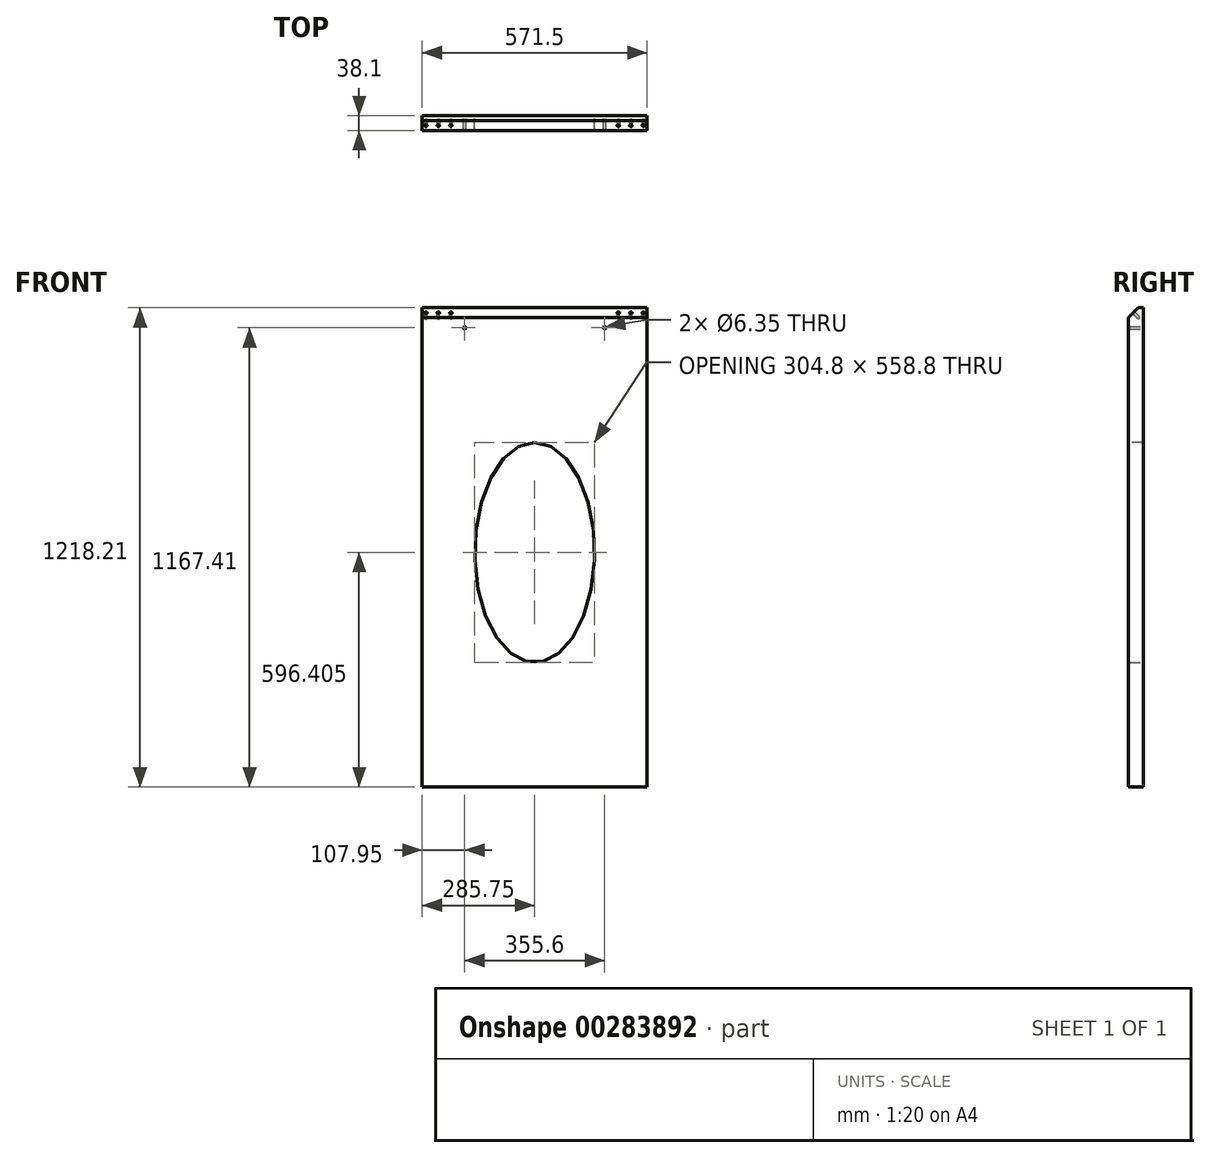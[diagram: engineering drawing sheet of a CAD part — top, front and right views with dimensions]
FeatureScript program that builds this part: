
annotation { "Feature Type Name" : "Feature", "Feature Type Description" : "" }
export const myFeature = defineFeature(function(context is Context, id is Id, definition is map)
    precondition{}
    {
        {
            var Q0;
            Q0=qCreatedBy(makeId("Front.planeOp"),FACE);
            var sketch = newSketch(context, id + "F0", { "sketchPlane" : qUnion([Q0])});
            skLineSegment(sketch, "E0.bottom", {"start": v(0, 0) * mm, "end": v(571.5, 0) * mm});
            skLineSegment(sketch, "E0.top", {"start": v(0, 1218.2) * mm, "end": v(571.5, 1218.2) * mm});
            skLineSegment(sketch, "E0.left", {"start": v(0, 0) * mm, "end": v(0, 1218.2) * mm});
            skLineSegment(sketch, "E0.right", {"start": v(571.5, 0) * mm, "end": v(571.5, 1218.2) * mm});
            skSolve(sketch);
        }
        {
            var Q0;
            Q0 = qSketchRegion(id + "F0", true);
            extrude(context, id + "F1", {"entities" : qUnion([Q0]), "depth" : 38.1 * mm});
        }
        {
            var Q0;
            Q0=makeQuery(id+"F1.opExtrude","CAP_EDGE",EDGE,{"disambiguationData":[OSD([sQuery(id+"F0.wireOp",EDGE,"E0.top")])],"isStart":false});
            chamfer(context, id + "F2", {"entities" : qUnion([Q0]), "width" : 25.4 * mm, "tangentPropagation" : true});
        }
        {
            var Q0;
            Q0=makeQuery(id+"F2.opChamfer","BLEND_FACE",FACE,{"disambiguationData":[OSD([sQuery(id+"F0.wireOp",EDGE,"E0.top")])]});
            var sketch = newSketch(context, id + "F3", { "sketchPlane" : qUnion([Q0])});
            skPoint(sketch, "E1", {"position": v(9.52, 834.46) * mm});
            skPoint(sketch, "E1.positionSnap0", {"position": v(0, 834.46) * mm});
            skPoint(sketch, "E2", {"position": v(41.27, 834.46) * mm});
            skPoint(sketch, "E3", {"position": v(73.03, 834.46) * mm});
            skPoint(sketch, "E4", {"position": v(285.75, 834.46) * mm});
            skLineSegment(sketch, "E5", {"start": v(285.75, 852.42) * mm, "end": v(285.75, 816.5) * mm, "construction": true});
            skPoint(sketch, "E6.MirrorP", {"position": v(498.47, 834.46) * mm});
            skPoint(sketch, "E7.MirrorP", {"position": v(530.22, 834.46) * mm});
            skPoint(sketch, "E8.MirrorP", {"position": v(561.97, 834.46) * mm});
            skSolve(sketch);
        }
        {
            var Q0;
            Q0=sQuery(id+"F3.wireOp",VERTEX,"E1");
            var Q1;
            Q1=sQuery(id+"F3.wireOp",VERTEX,"E2");
            var Q2;
            Q2=sQuery(id+"F3.wireOp",VERTEX,"E3");
            var Q3;
            Q3=sQuery(id+"F3.wireOp",VERTEX,"E6.MirrorP");
            var Q4;
            Q4=sQuery(id+"F3.wireOp",VERTEX,"E7.MirrorP");
            var Q5;
            Q5=sQuery(id+"F3.wireOp",VERTEX,"E8.MirrorP");
            var Q6;
            Q6=makeQuery(id+"F1.opExtrude","SWEPT_BODY",BODY,{"disambiguationData":[OSD([sQuery(id+"F0.wireOp",EDGE,"E0.bottom"),sQuery(id+"F0.wireOp",EDGE,"E0.top"),sQuery(id+"F0.wireOp",EDGE,"E0.left"),sQuery(id+"F0.wireOp",EDGE,"E0.right")])]});
            hole(context, id + "F4", {"style" : HoleStyle.SIMPLE, "endStyle" : HoleEndStyle.BLIND, "holeDiameter" : 6.35 * mm, "holeDepth" : 19.05 * mm, "tappedDepth" : 12.7 * mm, "tapClearance" : 3, "locations" : qUnion([Q0, Q1, Q2, Q3, Q4, Q5]), "scope" : qUnion([Q6])});
        }
        {
            var Q0;
            Q0=makeQuery(id+"F1.opExtrude","CAP_FACE",FACE,{"disambiguationData":[OSD([sQuery(id+"F0.wireOp",EDGE,"E0.bottom"),sQuery(id+"F0.wireOp",EDGE,"E0.top"),sQuery(id+"F0.wireOp",EDGE,"E0.left"),sQuery(id+"F0.wireOp",EDGE,"E0.right")])],"isStart":false});
            var sketch = newSketch(context, id + "F5", { "sketchPlane" : qUnion([Q0])});
            skPoint(sketch, "E9", {"position": v(19.05, 188.6) * mm});
            skPoint(sketch, "E10", {"position": v(552.45, 188.6) * mm});
            skLineSegment(sketch, "E11", {"start": v(0, 596.4) * mm, "end": v(571.5, 596.4) * mm});
            skLineSegment(sketch, "E12", {"start": v(285.75, 1192.8) * mm, "end": v(285.75, 0) * mm});
            skEllipse(sketch, "E13", {"center": v(285.75, 596.4) * mm, "majorRadius": 279.4 * mm, "minorRadius": 152.4 * mm, "majorAxis": v(0, 1)});
            skSolve(sketch);
        }
        {
            var Q0;
            {var subQ0=sQuery(id+"F5.wireOp",EDGE,"E13");var subQ1=sQuery(id+"F5.wireOp",EDGE,"E11");var subQ2=makeQuery(id+"F5.imprint","INTERSECT",VERTEX,{"disambiguationData":[OD(0.0)],"derivedFrom":[subQ1,subQ0]});Q0=makeQuery(id+"F5.imprint","IMPRINT",FACE,{"disambiguationData":[TD([[makeQuery(id+"F5.imprint","IMPRINT",EDGE,{"disambiguationData":[TD([[subQ2,-1.0]])],"derivedFrom":subQ1}),1.0]])]});}
            var Q1;
            {var subQ0=sQuery(id+"F5.wireOp",EDGE,"E12");var subQ1=sQuery(id+"F5.wireOp",EDGE,"E11");var subQ2=makeQuery(id+"F5.imprint","INTERSECT",VERTEX,{"derivedFrom":[subQ1,subQ0]});Q1=makeQuery(id+"F5.imprint","IMPRINT",FACE,{"disambiguationData":[TD([[makeQuery(id+"F5.imprint","IMPRINT",EDGE,{"disambiguationData":[TD([[subQ2,-1.0]])],"derivedFrom":subQ1}),1.0]])]});}
            var Q2;
            {var subQ0=sQuery(id+"F5.wireOp",EDGE,"E12");var subQ1=sQuery(id+"F5.wireOp",EDGE,"E11");var subQ2=makeQuery(id+"F5.imprint","INTERSECT",VERTEX,{"derivedFrom":[subQ1,subQ0]});Q2=makeQuery(id+"F5.imprint","IMPRINT",FACE,{"disambiguationData":[TD([[makeQuery(id+"F5.imprint","IMPRINT",EDGE,{"disambiguationData":[TD([[subQ2,-1.0]])],"derivedFrom":subQ1}),-1.0]])]});}
            var Q3;
            {var subQ0=sQuery(id+"F5.wireOp",EDGE,"E13");var subQ1=sQuery(id+"F5.wireOp",EDGE,"E11");var subQ2=makeQuery(id+"F5.imprint","INTERSECT",VERTEX,{"disambiguationData":[OD(0.0)],"derivedFrom":[subQ1,subQ0]});Q3=makeQuery(id+"F5.imprint","IMPRINT",FACE,{"disambiguationData":[TD([[makeQuery(id+"F5.imprint","IMPRINT",EDGE,{"disambiguationData":[TD([[subQ2,-1.0]])],"derivedFrom":subQ1}),-1.0]])]});}
            extrude(context, id + "F6", {"entities" : qUnion([Q0, Q1, Q2, Q3]), "operationType" : NewBodyOperationType.REMOVE, "endBound" : BoundingType.THROUGH_ALL, "oppositeDirection" : true, "depth" : 25.4 * mm});
        }
        {
            var Q0;
            Q0=makeQuery(id+"F1.opExtrude","CAP_FACE",FACE,{"disambiguationData":[OSD([sQuery(id+"F0.wireOp",EDGE,"E0.bottom"),sQuery(id+"F0.wireOp",EDGE,"E0.top"),sQuery(id+"F0.wireOp",EDGE,"E0.left"),sQuery(id+"F0.wireOp",EDGE,"E0.right")])],"isStart":true});
            var sketch = newSketch(context, id + "F7", { "sketchPlane" : qUnion([Q0])});
            skPoint(sketch, "E14", {"position": v(-463.55, 1167.4) * mm});
            skPoint(sketch, "E15.MirrorP", {"position": v(-107.95, 1167.4) * mm});
            skSolve(sketch);
        }
        {
            var Q0;
            Q0=sQuery(id+"F7.wireOp",VERTEX,"E14");
            var Q1;
            Q1=sQuery(id+"F7.wireOp",VERTEX,"E15.MirrorP");
            var Q2;
            Q2=makeQuery(id+"F1.opExtrude","SWEPT_BODY",BODY,{"disambiguationData":[OSD([sQuery(id+"F0.wireOp",EDGE,"E0.bottom"),sQuery(id+"F0.wireOp",EDGE,"E0.top"),sQuery(id+"F0.wireOp",EDGE,"E0.left"),sQuery(id+"F0.wireOp",EDGE,"E0.right")])]});
            hole(context, id + "F8", {"style" : HoleStyle.SIMPLE, "endStyle" : HoleEndStyle.THROUGH, "holeDiameter" : 6.35 * mm, "tappedDepth" : 12.7 * mm, "tapClearance" : 3, "locations" : qUnion([Q0, Q1]), "scope" : qUnion([Q2])});
        }
    });
